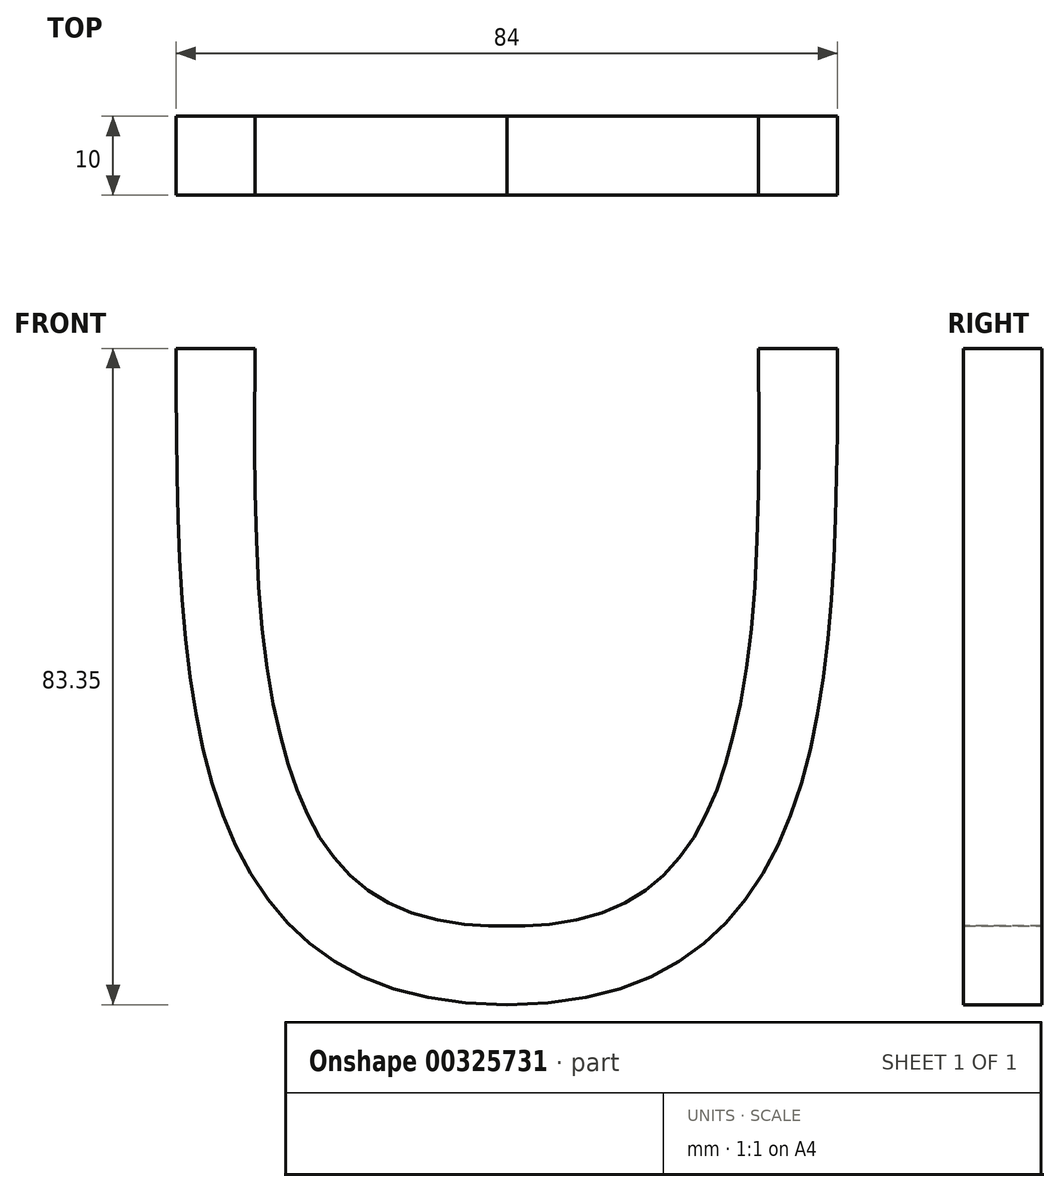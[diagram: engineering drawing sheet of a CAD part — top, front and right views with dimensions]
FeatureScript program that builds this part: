
annotation { "Feature Type Name" : "Feature", "Feature Type Description" : "" }
export const myFeature = defineFeature(function(context is Context, id is Id, definition is map)
    precondition{}
    {
        {
            var Q0;
            Q0=qCreatedBy(makeId("Front.planeOp"),FACE);
            var sketch = newSketch(context, id + "F0", { "sketchPlane" : qUnion([Q0])});
            skLineSegment(sketch, "E0", {"start": v(0, 0) * mm, "end": v(0, 57.1) * mm, "construction": true});
            skLineSegment(sketch, "E1", {"start": v(-42, 0) * mm, "end": v(0, 0) * mm, "construction": true});
            skLineSegment(sketch, "E2", {"start": v(0, 0) * mm, "end": v(42, 0) * mm, "construction": true});
            skLineSegment(sketch, "E3", {"start": v(42, 0) * mm, "end": v(42, 83.35) * mm, "construction": true});
            skFitSpline(sketch, "E4", {"points": [v(0, 0) * mm, v(42, 83.35) * mm], "startDerivative": vector(126, 0) * mm, "endDerivative": vector(0, 125.02) * mm});
            skFitSpline(sketch, "E5.MirrorCS", {"points": [v(0, 0) * mm, v(-42, 83.35) * mm], "startDerivative": vector(-126, 0) * mm, "endDerivative": vector(0, 125.02) * mm});
            skFitSpline(sketch, "E6.0", {"points": [v(0, 10) * mm, v(-2.21, 10) * mm, v(-6.23, 10.27) * mm, v(-11.12, 11.35) * mm, v(-15.04, 12.95) * mm, v(-18.25, 15) * mm, v(-20.99, 17.54) * mm, v(-23.4, 20.7) * mm, v(-25.51, 24.55) * mm, v(-27.32, 29.12) * mm, v(-28.81, 34.36) * mm, v(-30.36, 42.15) * mm, v(-31.52, 53.18) * mm, v(-32, 67.83) * mm, v(-32, 78.14) * mm, v(-32, 83.35) * mm]});
            skFitSpline(sketch, "E7.0", {"points": [v(0, 10) * mm, v(2.21, 10) * mm, v(6.23, 10.27) * mm, v(11.12, 11.35) * mm, v(15.04, 12.95) * mm, v(18.25, 15) * mm, v(20.99, 17.54) * mm, v(23.4, 20.7) * mm, v(25.51, 24.55) * mm, v(27.32, 29.12) * mm, v(28.81, 34.36) * mm, v(30.36, 42.15) * mm, v(31.52, 53.18) * mm, v(32, 67.83) * mm, v(32, 78.14) * mm, v(32, 83.35) * mm]});
            skLineSegment(sketch, "E8", {"start": v(-42, 83.35) * mm, "end": v(-32, 83.35) * mm});
            skLineSegment(sketch, "E9", {"start": v(32, 83.35) * mm, "end": v(42, 83.35) * mm});
            skPoint(sketch, "E10", {"position": v(-32, 80.48) * mm});
            skPoint(sketch, "E11", {"position": v(-31.95, 70.48) * mm});
            skPoint(sketch, "E12", {"position": v(-31.58, 56.98) * mm});
            skPoint(sketch, "E13", {"position": v(31.95, 70.48) * mm});
            skPoint(sketch, "E14", {"position": v(32, 80.48) * mm});
            skPoint(sketch, "E15", {"position": v(31.58, 56.98) * mm});
            skPoint(sketch, "E16", {"position": v(-16.43, 70.48) * mm});
            skPoint(sketch, "E17", {"position": v(16.45, 70.48) * mm});
            skLineSegment(sketch, "E18", {"start": v(-31.95, 70.48) * mm, "end": v(-16.43, 70.48) * mm});
            skLineSegment(sketch, "E19", {"start": v(-31.58, 56.98) * mm, "end": v(-16.43, 70.48) * mm});
            skLineSegment(sketch, "E20", {"start": v(31.58, 56.98) * mm, "end": v(16.45, 70.48) * mm});
            skLineSegment(sketch, "E21", {"start": v(31.95, 70.48) * mm, "end": v(16.45, 70.48) * mm});
            skSolve(sketch);
        }
        {
            var Q0;
            Q0 = qSketchRegion(id + "F0", true);
            extrude(context, id + "F1", {"entities" : qUnion([Q0]), "endBound" : BoundingType.SYMMETRIC, "depth" : 10 * mm});
        }
    });
